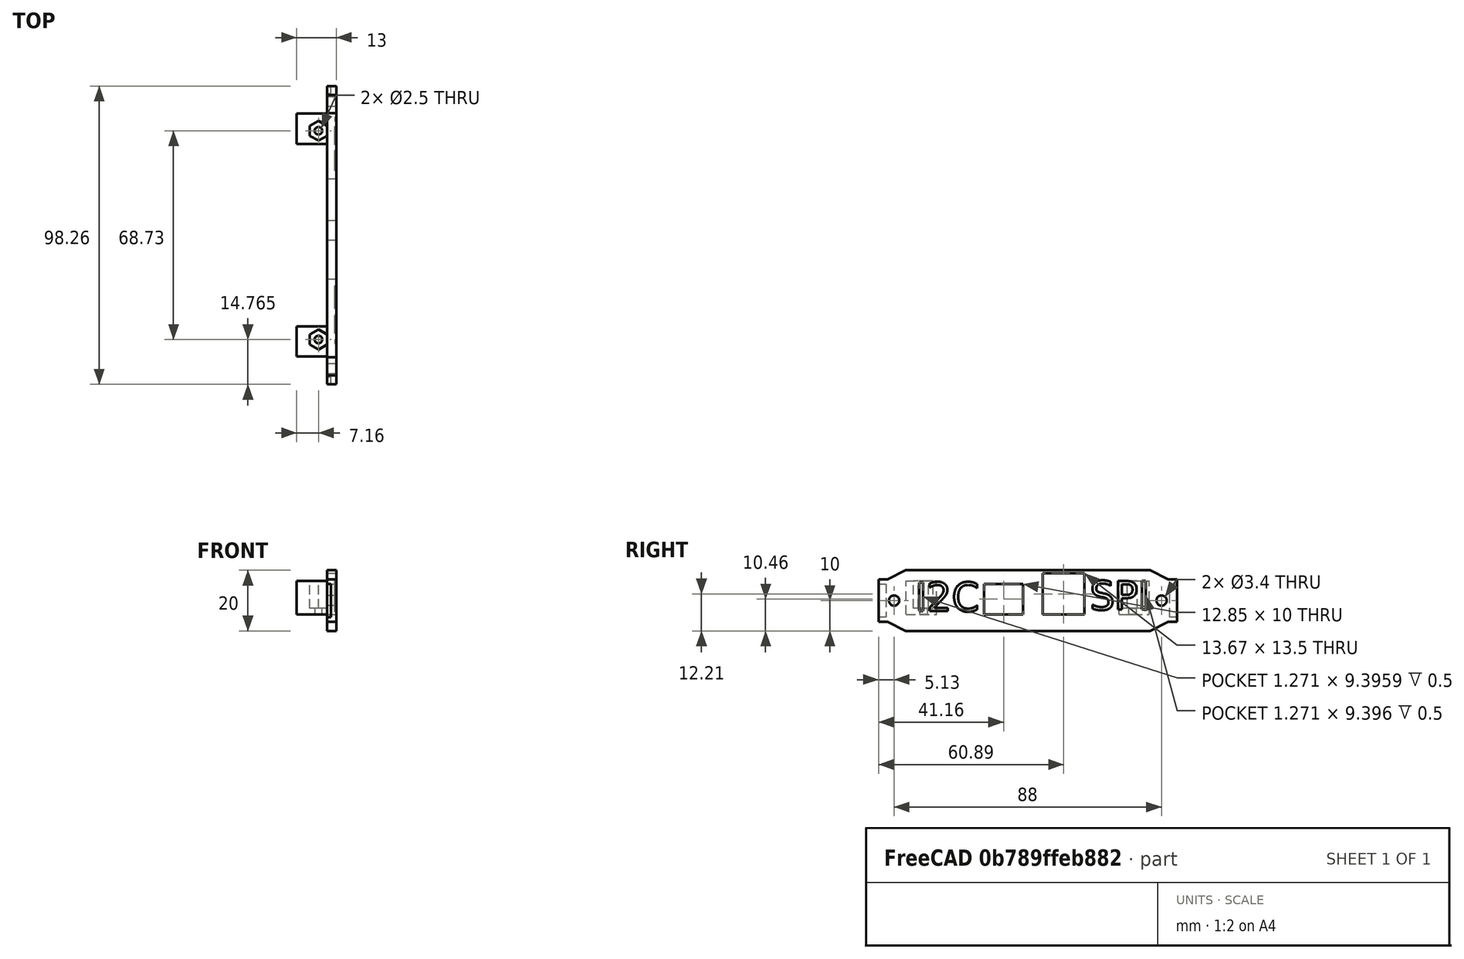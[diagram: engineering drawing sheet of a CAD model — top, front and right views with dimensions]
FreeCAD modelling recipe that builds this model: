
FCSTD DOCUMENT  (FreeCAD 0.19R24291 (Git))
Label: FacePlate_FCNative_v1
License: All rights reserved
LicenseURL: http://en.wikipedia.org/wiki/All_rights_reserved
objects: TechDraw::DrawViewDimension×21, Sketcher::SketchObject×5, PartDesign::Pocket×5, TechDraw::DrawProjGroupItem×4, PartDesign::Pad×2, Part::Part2DObjectPython×2, Mesh::Feature×1, TechDraw::DrawSVGTemplate×1, PartDesign::Body×1, TechDraw::DrawProjGroup×1, TechDraw::DrawPage×1
note: 22 computed .brp shape members not serialized (recipe doc carries the construction recipe); baked Part::Feature solids carry a one-line shape summary decoded from their .brp

FEATURE [Mesh::Feature] PolyVent_SPI_Controller_faceplate_v8  label="PolyVent_SPI_Controller-faceplate v8"
  Placement = pos=(-198.5,104.98,-6.2) rot=(0,0,1;0rad)
FEATURE [Sketcher::SketchObject] Sketch  label="SketchFacePlateBlank"
  FullyConstrained = false
  MapMode = 5
  Placement = pos=(0,0,0) rot=(0.57735,0.57735,0.57735;2.0944rad)
  Support = -> [YZ_Plane]
  sketch-geometry (43):
    g0: Circle CenterX=-44 CenterY=0 CenterZ=0 NormalX=0 NormalY=0 NormalZ=1 AngleXU=0 Radius=1.7
    g1: Circle CenterX=44 CenterY=0 CenterZ=0 NormalX=0 NormalY=0 NormalZ=1 AngleXU=0 Radius=1.7
    g2: LineSegment StartX=-49.13 StartY=6.957 StartZ=0 EndX=-49.13 EndY=-6.957 EndZ=0
    g3: LineSegment StartX=-49.13 StartY=6.957 StartZ=0 EndX=-46.13 EndY=6.957 EndZ=0
    g4: LineSegment StartX=-46.13 StartY=6.957 StartZ=0 EndX=-40.2064 EndY=10 EndZ=0
    g5: LineSegment StartX=-49.13 StartY=-6.957 StartZ=0 EndX=-46.13 EndY=-6.957 EndZ=0
    g6: LineSegment StartX=-46.13 StartY=-6.957 StartZ=0 EndX=-40.2064 EndY=-10 EndZ=0
    g7: LineSegment StartX=-40.2064 StartY=10 StartZ=0 EndX=40.2064 EndY=10 EndZ=0
    g8: LineSegment StartX=40.2064 StartY=10 StartZ=0 EndX=46.13 EndY=6.957 EndZ=0
    g9: LineSegment StartX=46.13 StartY=6.957 StartZ=0 EndX=49.13 EndY=6.957 EndZ=0
    g10: LineSegment StartX=49.13 StartY=6.957 StartZ=0 EndX=49.13 EndY=-6.957 EndZ=0
    g11: LineSegment StartX=49.13 StartY=-6.957 StartZ=0 EndX=46.13 EndY=-6.957 EndZ=0
    g12: LineSegment StartX=46.13 StartY=-6.957 StartZ=0 EndX=40.2064 EndY=-10 EndZ=0
    g13: LineSegment StartX=40.2064 StartY=-10 StartZ=0 EndX=-40.2064 EndY=-10 EndZ=0
    g14: ArcOfCircle CenterX=-46.13 CenterY=-6.957 CenterZ=0 NormalX=0 NormalY=0 NormalZ=1 AngleXU=0 Radius=3 StartAngle=3.14159 EndAngle=5.80863
    g15: LineSegment StartX=-40 StartY=-4.54 StartZ=0 EndX=40 EndY=-4.54 EndZ=0
    g16: LineSegment StartX=40 StartY=-4.54 StartZ=0 EndX=40 EndY=-6.14 EndZ=0
    g17: LineSegment StartX=40 StartY=-6.14 StartZ=0 EndX=-40 EndY=-6.14 EndZ=0
    g18: LineSegment StartX=-40 StartY=-6.14 StartZ=0 EndX=-40 EndY=-4.54 EndZ=0
    g19: LineSegment StartX=-40 StartY=-4.54 StartZ=0 EndX=-30 EndY=-4.54 EndZ=0
    g20: LineSegment StartX=-30 StartY=-4.54 StartZ=0 EndX=-30 EndY=6.46 EndZ=0
    g21: LineSegment StartX=-30 StartY=6.46 StartZ=0 EndX=-40 EndY=6.46 EndZ=0
    g22: LineSegment StartX=-40 StartY=6.46 StartZ=0 EndX=-40 EndY=-4.54 EndZ=0
    g23: LineSegment StartX=40 StartY=-4.54 StartZ=0 EndX=30 EndY=-4.54 EndZ=0
    g24: LineSegment StartX=30 StartY=-4.54 StartZ=0 EndX=30 EndY=6.46 EndZ=0
    g25: LineSegment StartX=30 StartY=6.46 StartZ=0 EndX=40 EndY=6.46 EndZ=0
    g26: LineSegment StartX=40 StartY=6.46 StartZ=0 EndX=40 EndY=-4.54 EndZ=0
    g27: LineSegment StartX=31.113 StartY=6.46 StartZ=0 EndX=37.637 EndY=6.46 EndZ=0
    g28: LineSegment StartX=37.637 StartY=6.46 StartZ=0 EndX=37.637 EndY=-2.54 EndZ=0
    g29: LineSegment StartX=37.637 StartY=-2.54 StartZ=0 EndX=31.113 EndY=-2.54 EndZ=0
    g30: LineSegment StartX=31.113 StartY=-2.54 StartZ=0 EndX=31.113 EndY=6.46 EndZ=0
    g31: LineSegment StartX=34.375 StartY=6.46 StartZ=0 EndX=34.375 EndY=-4.54 EndZ=0
    g32: LineSegment StartX=-34.375 StartY=6.46 StartZ=0 EndX=-34.375 EndY=-4.54 EndZ=0
    g33: LineSegment StartX=37.637 StartY=18.8909 StartZ=0 EndX=36.006 EndY=21.7159 EndZ=0
    g34: LineSegment StartX=36.006 StartY=21.7159 StartZ=0 EndX=32.744 EndY=21.7159 EndZ=0
    g35: LineSegment StartX=32.744 StartY=21.7159 StartZ=0 EndX=31.113 EndY=18.8909 EndZ=0
    g36: LineSegment StartX=31.113 StartY=18.8909 StartZ=0 EndX=32.744 EndY=16.0659 EndZ=0
    g37: LineSegment StartX=32.744 StartY=16.0659 StartZ=0 EndX=36.006 EndY=16.0659 EndZ=0
    g38: LineSegment StartX=36.006 StartY=16.0659 StartZ=0 EndX=37.637 EndY=18.8909 EndZ=0
    g39: Circle CenterX=34.375 CenterY=18.8909 CenterZ=0 NormalX=0 NormalY=0 NormalZ=1 AngleXU=0 Radius=3.26203
    g40: LineSegment StartX=-49.13 StartY=5.46 StartZ=0 EndX=-46.63 EndY=5.46 EndZ=0
    g41: LineSegment StartX=-46.63 StartY=5.46 StartZ=0 EndX=-46.63 EndY=-5.46 EndZ=0
    g42: LineSegment StartX=-46.63 StartY=-5.46 StartZ=0 EndX=-49.13 EndY=-5.46 EndZ=0
  constraints (119):
    c: Vertical(g2)
    c: Coincident(g3,g2)
    c: Horizontal(g3)
    c: Coincident(g4,g3)
    c: Coincident(g5,g2)
    c: Horizontal(g5)
    c: Coincident(g6,g5)
    c: Vertical(g4,g6)
    c: Vertical(g5,g3)
    c: Coincident(g7,g4)
    c: Horizontal(g7)
    c: Coincident(g8,g7)
    c: Coincident(g9,g8)
    c: Horizontal(g9)
    c: Coincident(g10,g9)
    c: Vertical(g10)
    c: Coincident(g11,g10)
    c: Horizontal(g11)
    c: Coincident(g12,g11)
    c: Coincident(g13,g12)
    c: Coincident(g13,g6)
    c: Horizontal(g13)
    c: Equal(g6,g4)
    c: Equal(g4,g8)
    c: Equal(g8,g12)
    c: Equal(g5,g11)
    c: Vertical(g11,g8)
    c: Horizontal(g0,g1)
    c: Horizontal(g5,g11)
    c: Horizontal(g3,g8)
    c: DistanceY(g5) = -6.957
    c: DistanceX(g5,g5) = 3
    c: DistanceY(g2,g2) = 13.914
    c: DistanceX(g5,g6) = 5.92358
    c: DistanceY(g6,g4) = 20
    c: Coincident(g14,g5)
    c: PointOnObject(g14,g6)
    c: Angle(g14) = 2.66704
    c: Diameter(g0) = 3.4
    c: Equal(g1,g0)
    c: DistanceX(g2,g10) = 98.26  'L1'
    c: PointOnObject(g1,g-1)
    c: Coincident(g15,g16)
    c: Coincident(g16,g17)
    c: Coincident(g17,g18)
    c: Coincident(g18,g15)
    c: Horizontal(g15)
    c: Vertical(g16)
    c: Vertical(g18)
    c: DistanceY(g15) = -4.54  'PCB_top_center_offset'
    c: DistanceY(g16,g16) = 1.6  'PCB_tickness'
    c: DistanceX(g17,g17) = 80  'PCB_width'
    c: Symmetric(g16,g17,g-2)
    c: Coincident(g14,g2)
    c: Coincident(g19,g20)
    c: Coincident(g20,g21)
    c: Coincident(g21,g22)
    c: Coincident(g22,g19)
    c: Horizontal(g19)
    c: Horizontal(g21)
    c: Vertical(g20)
    c: Vertical(g22)
    c: Coincident(g19,g15)
    c: Coincident(g23,g24)
    c: Coincident(g24,g25)
    c: Coincident(g25,g26)
    c: Coincident(g26,g23)
    c: Horizontal(g23)
    c: Horizontal(g25)
    c: Vertical(g24)
    c: Vertical(g26)
    c: Coincident(g23,g15)
    c: Horizontal(g20,g24)
    c: Equal(g21,g25)
    c: DistanceY(g26,g26) = 11  'PCB_mounting_tab_height'
    c: DistanceX(g25,g25) = 10  'PCB_mount_tab_width'
    c: Coincident(g27,g28)
    c: Coincident(g28,g29)
    c: Coincident(g29,g30)
    c: Coincident(g30,g27)
    c: Horizontal(g27)
    c: Vertical(g28)
    c: Vertical(g30)
    c: PointOnObject(g27,g25)
    c: DistanceY(g23,g29) = 2  'bore_length'
    c: PointOnObject(g31,g25)
    c: PointOnObject(g31,g15)
    c: Vertical(g31)
    c: Symmetric(g29,g28,g31)
    c: PointOnObject(g32,g21)
    c: Vertical(g32)
    c: Symmetric(g32,g31,g-2)
    c: DistanceX(g32,g31) = 68.75  'PCB_hole_distance_width'
    c: Coincident(g33,g34)
    c: Coincident(g34,g35)
    c: Coincident(g35,g36)
    c: Coincident(g36,g37)
    c: Coincident(g37,g38)
    c: Coincident(g38,g33)
    c: Equal(g33, g34-g38) x5
    c: PointOnObject(g33,g39)
    c: PointOnObject(g34,g39)
    c: PointOnObject(g35,g39)
    c: PointOnObject(g36,g39)
    c: PointOnObject(g37,g39)
    c: PointOnObject(g38,g39)
    c: Vertical(g27,g35)
    c: Horizontal(g35,g33)
    c: Vertical(g33,g27)
    c: DistanceY(g37,g33) = 5.65  'nut_spanner_dim'
    c: PointOnObject(g40,g2)
    c: Horizontal(g40)
    c: Coincident(g41,g40)
    c: Coincident(g42,g41)
    c: PointOnObject(g42,g2)
    c: Horizontal(g42)
    c: DistanceX(g42,g42) = 2.5  'L3'
    c: Symmetric(g41,g40,g-1)
    c: DistanceY(g41,g41) = 10.92  'L2'
FEATURE [PartDesign::Pad] Pad  label="PadFacePlateBlank"
  Direction = (1,-2e-16,3e-16)
  Length = 3
  Length2 = 10
  Placement = pos=(0,0,0) rot=(0.57735,0.57735,0.57735;2.0944rad)
  Profile = -> Sketch
  Type = 0
FEATURE [Sketcher::SketchObject] Sketch001  label="SketchPCBMount"
  AttachmentOffset = pos=(0,0,-4.54) rot=(0,0,1;0rad)
  FullyConstrained = false
  MapMode = 5
  Placement = pos=(0,0,-4.54) rot=(0,0,1;0rad)
  Support = -> [XY_Plane]
  expr: .AttachmentOffset.Base.z = Sketch.Constraints.PCB_top_center_offset
  expr: Constraints[20] = Sketch.Constraints.PCB_mount_tab_width
  expr: Constraints[39] = Sketch.Constraints.PCB_width
  sketch-geometry (15):
    g0: LineSegment StartX=0 StartY=40 StartZ=0 EndX=-10 EndY=40 EndZ=0
    g1: LineSegment StartX=-10 StartY=40 StartZ=0 EndX=-10 EndY=30 EndZ=0
    g2: LineSegment StartX=-10 StartY=30 StartZ=0 EndX=0 EndY=30 EndZ=0
    g3: LineSegment StartX=0 StartY=30 StartZ=0 EndX=0 EndY=40 EndZ=0
    g4: LineSegment StartX=0 StartY=-30 StartZ=0 EndX=-10 EndY=-30 EndZ=0
    g5: LineSegment StartX=-10 StartY=-30 StartZ=0 EndX=-10 EndY=-40 EndZ=0
    g6: LineSegment StartX=-10 StartY=-40 StartZ=0 EndX=0 EndY=-40 EndZ=0
    g7: LineSegment StartX=0 StartY=-40 StartZ=0 EndX=0 EndY=-30 EndZ=0
    g8: Circle CenterX=-2.84 CenterY=-34.365 CenterZ=0 NormalX=0 NormalY=0 NormalZ=1 AngleXU=0 Radius=1.25
    g9: Circle CenterX=-2.84 CenterY=34.365 CenterZ=0 NormalX=0 NormalY=0 NormalZ=1 AngleXU=0 Radius=1.25
    g10: LineSegment StartX=0 StartY=0 StartZ=0 EndX=-11.2307 EndY=0 EndZ=0
    g11: LineSegment StartX=-136.907 StartY=40 StartZ=0 EndX=-12.6927 EndY=40 EndZ=0
    g12: LineSegment StartX=-12.6927 StartY=40 StartZ=0 EndX=-12.6927 EndY=-40 EndZ=0
    g13: LineSegment StartX=-12.6927 StartY=-40 StartZ=0 EndX=-136.907 EndY=-40 EndZ=0
    g14: LineSegment StartX=-136.907 StartY=-40 StartZ=0 EndX=-136.907 EndY=40 EndZ=0
  constraints (40):
    c: Coincident(g0,g1)
    c: Coincident(g1,g2)
    c: Coincident(g2,g3)
    c: Coincident(g3,g0)
    c: Horizontal(g0)
    c: Horizontal(g2)
    c: Vertical(g1)
    c: Vertical(g3)
    c: PointOnObject(g0,g-2)
    c: Coincident(g4,g5)
    c: Coincident(g5,g6)
    c: Coincident(g6,g7)
    c: Coincident(g7,g4)
    c: Horizontal(g4)
    c: Horizontal(g6)
    c: Vertical(g5)
    c: Vertical(g7)
    c: PointOnObject(g4,g-2)
    c: Equal(g8,g9)
    c: DistanceX(g2,g2) = 10
    c: DistanceY(g1,g1) = 10
    c: Diameter(g9) = 2.5
    c: PointOnObject(g10,g-2)
    c: Symmetric(g8,g9,g10)
    c: Horizontal(g10)
    c: DistanceX(g8,g10) = 2.84
    c: DistanceY(g8,g9) = 68.73
    c: DistanceY(g4,g1) = 60
    c: Symmetric(g4,g1,g10)
    c: Equal(g1,g5)
    c: PointOnObject(g10,g-1)
    c: Coincident(g11,g12)
    c: Coincident(g12,g13)
    c: Coincident(g13,g14)
    c: Coincident(g14,g11)
    c: Horizontal(g11)
    c: Horizontal(g13)
    c: Vertical(g12)
    c: Symmetric(g13,g11,g-1)
    c: DistanceY(g14,g14) = 80
FEATURE [PartDesign::Pad] Pad001  label="PadPCBMount"
  BaseFeature = -> Pad
  Direction = (0,0,1)
  Length = 11
  Length2 = 10
  Placement = pos=(0,0,0) rot=(0.57735,0.57735,0.57735;2.0944rad)
  Profile = -> Sketch001
  Type = 0
  expr: Length = Sketch.Constraints.PCB_mounting_tab_height
FEATURE [Sketcher::SketchObject] Sketch002  label="SketchNuts"
  AttachmentOffset = pos=(0,0,-2.54) rot=(0,0,1;0rad)
  FullyConstrained = false
  MapMode = 5
  Placement = pos=(0,0,-2.54) rot=(0,0,1;0rad)
  Support = -> [XY_Plane]
  expr: .AttachmentOffset.Base.z = Sketch.Constraints.PCB_top_center_offset + Sketch.Constraints.bore_length
  expr: Constraints[18] = Sketch.Constraints.nut_spanner_dim
  expr: Constraints[50] = Sketch.Constraints.PCB_hole_distance_width
  expr: Constraints[51] = Sketch.Constraints.PCB_width
  sketch-geometry (18):
    g0: LineSegment StartX=-0.015 StartY=36.006 StartZ=0 EndX=-2.84 EndY=37.637 EndZ=0
    g1: LineSegment StartX=-2.84 StartY=37.637 StartZ=0 EndX=-5.665 EndY=36.006 EndZ=0
    g2: LineSegment StartX=-5.665 StartY=36.006 StartZ=0 EndX=-5.665 EndY=32.744 EndZ=0
    g3: LineSegment StartX=-5.665 StartY=32.744 StartZ=0 EndX=-2.84 EndY=31.113 EndZ=0
    g4: LineSegment StartX=-2.84 StartY=31.113 StartZ=0 EndX=-0.015 EndY=32.744 EndZ=0
    g5: LineSegment StartX=-0.015 StartY=32.744 StartZ=0 EndX=-0.015 EndY=36.006 EndZ=0
    g6: Circle CenterX=-2.84 CenterY=34.375 CenterZ=0 NormalX=0 NormalY=0 NormalZ=1 AngleXU=0 Radius=3.26203
    g7: LineSegment StartX=-73.2053 StartY=40 StartZ=0 EndX=0 EndY=40 EndZ=0
    g8: LineSegment StartX=0 StartY=40 StartZ=0 EndX=0 EndY=-40 EndZ=0
    g9: LineSegment StartX=0 StartY=-40 StartZ=0 EndX=-73.2053 EndY=-40 EndZ=0
    g10: LineSegment StartX=-73.2053 StartY=-40 StartZ=0 EndX=-73.2053 EndY=40 EndZ=0
    g11: LineSegment StartX=-0.015 StartY=-36.006 StartZ=0 EndX=-0.015 EndY=-32.744 EndZ=0
    g12: LineSegment StartX=-0.015 StartY=-32.744 StartZ=0 EndX=-2.84 EndY=-31.113 EndZ=0
    g13: LineSegment StartX=-2.84 StartY=-31.113 StartZ=0 EndX=-5.665 EndY=-32.744 EndZ=0
    g14: LineSegment StartX=-5.665 StartY=-32.744 StartZ=0 EndX=-5.665 EndY=-36.006 EndZ=0
    g15: LineSegment StartX=-5.665 StartY=-36.006 StartZ=0 EndX=-2.84 EndY=-37.637 EndZ=0
    g16: LineSegment StartX=-2.84 StartY=-37.637 StartZ=0 EndX=-0.015 EndY=-36.006 EndZ=0
    g17: Circle CenterX=-2.84 CenterY=-34.375 CenterZ=0 NormalX=0 NormalY=0 NormalZ=1 AngleXU=0 Radius=3.26203
  constraints (45):
    c: Coincident(g0,g1)
    c: Coincident(g1,g2)
    c: Coincident(g2,g3)
    c: Coincident(g3,g4)
    c: Coincident(g4,g5)
    c: Coincident(g5,g0)
    c: Equal(g0, g1-g5) x5
    c: PointOnObject(g0,g6)
    c: PointOnObject(g1,g6)
    c: PointOnObject(g2,g6)
    c: PointOnObject(g3,g6)
    c: PointOnObject(g4,g6)
    c: PointOnObject(g5,g6)
    c: Vertical(g5)
    c: DistanceX(g2,g4) = 5.65
    c: DistanceY(g-1,g6) = 34.375
    c: DistanceX(g6,g-1) = 2.84
    c: Coincident(g7,g8)
    c: Coincident(g8,g9)
    c: Coincident(g9,g10)
    c: Coincident(g10,g7)
    c: Horizontal(g7)
    c: Horizontal(g9)
    c: Vertical(g8)
    c: PointOnObject(g8,g-2)
    c: Symmetric(g9,g7,g-1)
    c: Coincident(g11,g12)
    c: Coincident(g12,g13)
    c: Coincident(g13,g14)
    c: Coincident(g14,g15)
    c: Coincident(g15,g16)
    c: Coincident(g16,g11)
    c: Equal(g11, g12-g16) x5
    c: PointOnObject(g11,g17)
    c: PointOnObject(g12,g17)
    c: PointOnObject(g13,g17)
    c: PointOnObject(g14,g17)
    c: PointOnObject(g15,g17)
    c: PointOnObject(g16,g17)
    c: Vertical(g11)
    c: Equal(g17,g6)
    c: Symmetric(g17,g6,g-1)
    c: DistanceY(g17,g6) = 68.75
    c: DistanceY(g10,g10) = 80
    c: DistanceY(g6,g7) = 5.625
FEATURE [PartDesign::Pocket] Pocket  label="Pocket_nut"
  BaseFeature = -> Pad001
  Length = 5
  Length2 = 5
  Placement = pos=(0,0,0) rot=(0.57735,0.57735,0.57735;2.0944rad)
  Profile = -> Sketch002
  Reversed = true
  Type = 1
FEATURE [Sketcher::SketchObject] Sketch003  label="SketchExtraction"
  FullyConstrained = true
  MapMode = 5
  Placement = pos=(0,0,0) rot=(0.57735,0.57735,0.57735;2.0944rad)
  Support = -> [YZ_Plane]
  expr: Constraints[19] = Sketch.Constraints.L1
  expr: Constraints[20] = Sketch.Constraints.L2
  expr: Constraints[21] = Sketch.Constraints.L3
  sketch-geometry (8):
    g0: LineSegment StartX=-49.13 StartY=5.46 StartZ=0 EndX=-46.63 EndY=5.46 EndZ=0
    g1: LineSegment StartX=-46.63 StartY=5.46 StartZ=0 EndX=-46.63 EndY=-5.46 EndZ=0
    g2: LineSegment StartX=-46.63 StartY=-5.46 StartZ=0 EndX=-49.13 EndY=-5.46 EndZ=0
    g3: LineSegment StartX=-49.13 StartY=-5.46 StartZ=0 EndX=-49.13 EndY=5.46 EndZ=0
    g4: LineSegment StartX=46.63 StartY=5.46 StartZ=0 EndX=49.13 EndY=5.46 EndZ=0
    g5: LineSegment StartX=49.13 StartY=5.46 StartZ=0 EndX=49.13 EndY=-5.46 EndZ=0
    g6: LineSegment StartX=49.13 StartY=-5.46 StartZ=0 EndX=46.63 EndY=-5.46 EndZ=0
    g7: LineSegment StartX=46.63 StartY=-5.46 StartZ=0 EndX=46.63 EndY=5.46 EndZ=0
  constraints (22):
    c: Coincident(g0,g1)
    c: Coincident(g1,g2)
    c: Coincident(g2,g3)
    c: Coincident(g3,g0)
    c: Horizontal(g0)
    c: Horizontal(g2)
    c: Vertical(g1)
    c: Coincident(g4,g5)
    c: Coincident(g5,g6)
    c: Coincident(g6,g7)
    c: Coincident(g7,g4)
    c: Horizontal(g4)
    c: Horizontal(g6)
    c: Vertical(g5)
    c: Vertical(g7)
    c: Horizontal(g0,g4)
    c: Symmetric(g0,g5,g-1)
    c: Symmetric(g2,g0,g-1)
    c: Equal(g0,g4)
    c: DistanceX(g2,g5) = 98.26
    c: DistanceY(g1,g1) = 10.92
    c: DistanceX(g2,g2) = 2.5
FEATURE [PartDesign::Pocket] Pocket001  label="PocketExtraction"
  BaseFeature = -> Pocket
  Length = 1.25
  Length2 = 5
  Placement = pos=(0,0,0) rot=(0.57735,0.57735,0.57735;2.0944rad)
  Profile = -> Sketch003
  Reversed = true
  Type = 0
FEATURE [TechDraw::DrawSVGTemplate] Template
  EditableTexts = Approved1=20230622 1317; Approved2=Approved 2; CheckedBy=Checked By; Code=Code; CompanyAddress=Publnv.org; CompanyName=PUblicInvention; DrawingNumber=Drawing Number; DrawingTitle1=PolyVentFacePlate; DrawingTitle2=FacePlate_FCNative_v1_SPI_Controller.p[df; DrawingTitle3=Drawing Title 3; DrawnBy=(Forrest) Lee Erickson; Revision=Rev; Scale=Scale 1:1; Sheet=Sheet 1 of 1
  Height = 215.9
  Orientation = 1
  Width = 279.4
FEATURE [Sketcher::SketchObject] Sketch004  label="SketchFacePlateHoles"
  FullyConstrained = false
  MapMode = 5
  Placement = pos=(0,0,0) rot=(0.57735,0.57735,0.57735;2.0944rad)
  Support = -> [YZ_Plane]
  sketch-geometry (11):
    g0: GeomPoint X=0 Y=0 Z=0
    g1: LineSegment StartX=4.925 StartY=8.96 StartZ=0 EndX=18.595 EndY=8.96 EndZ=0
    g2: LineSegment StartX=18.595 StartY=8.96 StartZ=0 EndX=18.595 EndY=-4.54 EndZ=0
    g3: LineSegment StartX=18.595 StartY=-4.54 StartZ=0 EndX=4.925 EndY=-4.54 EndZ=0
    g4: LineSegment StartX=4.925 StartY=-4.54 StartZ=0 EndX=4.925 EndY=8.96 EndZ=0
    g5: LineSegment StartX=-14.395 StartY=5.46 StartZ=0 EndX=-1.545 EndY=5.46 EndZ=0
    g6: LineSegment StartX=-1.545 StartY=5.46 StartZ=0 EndX=-1.545 EndY=-4.54 EndZ=0
    g7: LineSegment StartX=-1.545 StartY=-4.54 StartZ=0 EndX=-14.395 EndY=-4.54 EndZ=0
    g8: LineSegment StartX=-14.395 StartY=-4.54 StartZ=0 EndX=-14.395 EndY=5.46 EndZ=0
    g9: GeomPoint X=-7.97 Y=0.46 Z=0
    g10: GeomPoint X=11.76 Y=2.21 Z=0
  constraints (27):
    c: Coincident(g1,g2)
    c: Coincident(g2,g3)
    c: Coincident(g3,g4)
    c: Coincident(g4,g1)
    c: Horizontal(g1)
    c: Horizontal(g3)
    c: Vertical(g2)
    c: Vertical(g4)
    c: Coincident(g5,g6)
    c: Coincident(g6,g7)
    c: Coincident(g7,g8)
    c: Coincident(g8,g5)
    c: Horizontal(g5)
    c: Horizontal(g7)
    c: Vertical(g6)
    c: Vertical(g8)
    c: PointOnObject(g0,g-2)
    c: Symmetric(g7,g5,g9)
    c: Symmetric(g3,g1,g10)
    c: Horizontal(g6,g3)
    c: DistanceX(g5,g5) = 12.85
    c: DistanceY(g8,g8) = 10
    c: DistanceX(g1,g1) = 13.67
    c: DistanceY(g2,g2) = 13.5
    c: DistanceX(g9,g0) = 7.97
    c: DistanceX(g0,g10) = 11.76
    c: DistanceY(g6,g-1) = 4.54
FEATURE [PartDesign::Pocket] Pocket002  label="PocketFacePlateHoles"
  BaseFeature = -> Pocket001
  Length = 5
  Length2 = 100
  Placement = pos=(0,0,0) rot=(0.57735,0.57735,0.57735;2.0944rad)
  Profile = -> Sketch004
  Reversed = true
  Type = 1
FEATURE [Part::Part2DObjectPython] ShapeString  label="ShapeStringSPI"  # Draft 2D object (typed FeaturePython)
  FontFile = <path>
  Placement = pos=(3,20.3978,-2.95812) rot=(0.57735,0.57735,0.57735;2.0944rad)
  Size = 10
  String = SPI
  Tracking = 0
FEATURE [PartDesign::Pocket] Pocket003  label="PocketSPI"
  BaseFeature = -> Pocket002
  Length = 0.5
  Length2 = 100
  Placement = pos=(0,0,0) rot=(0.57735,0.57735,0.57735;2.0944rad)
  Profile = -> ShapeString
  Type = 0
FEATURE [Part::Part2DObjectPython] ShapeString001  label="ShapeStringI2C"  # Draft 2D object (typed FeaturePython)
  FontFile = <path>
  Placement = pos=(3,-37.0721,-3.45493) rot=(0.57735,0.57735,0.57735;2.0944rad)
  Size = 10
  String = I2C
  Tracking = 0
FEATURE [PartDesign::Pocket] Pocket004  label="PocketI2C"
  BaseFeature = -> Pocket003
  Length = 0.5
  Length2 = 100
  Placement = pos=(0,0,0) rot=(0.57735,0.57735,0.57735;2.0944rad)
  Profile = -> ShapeString001
  Type = 0
FEATURE [PartDesign::Body] Body
  Group = -> [Sketch,Pad,Sketch001,Pad001,Sketch002,Pocket,Sketch003,Pocket001,Sketch004,Pocket002,ShapeString,Pocket003,ShapeString001,Pocket004]
  Origin = -> Origin
  Tip = -> Pocket004
FEATURE [TechDraw::DrawProjGroupItem] ProjItem  label="Front"
  CoarseView = false
  Direction = (1,0,0)
  Focus = 100
  HardHidden = false
  IsoCount = 0
  IsoHidden = false
  IsoVisible = false
  LockPosition = true
  Perspective = false
  Rotation = 0
  RotationVector = (0,1,0)
  ScaleType = 2
  SeamHidden = false
  SeamVisible = true
  SmoothHidden = false
  SmoothVisible = true
  Source = -> [Body]
  Type = 0
  X = 0
  XDirection = (0,1,0)
  Y = 0
FEATURE [TechDraw::DrawProjGroupItem] ProjItem001  label="FrontTopRight"
  CoarseView = false
  Direction = (0.57735,0.57735,0.57735)
  Focus = 100
  HardHidden = false
  IsoCount = 0
  IsoHidden = false
  IsoVisible = false
  LockPosition = true
  Perspective = false
  Rotation = 0
  RotationVector = (1,0,0)
  ScaleType = 2
  SeamHidden = false
  SeamVisible = true
  SmoothHidden = false
  SmoothVisible = true
  Source = -> [Body]
  Type = 7
  X = 115.005
  XDirection = (-0.707107,0.707107,0)
  Y = 72.8098
FEATURE [TechDraw::DrawProjGroupItem] ProjItem002  label="Top"
  CoarseView = false
  Direction = (0,0,1)
  Focus = 100
  HardHidden = false
  IsoCount = 0
  IsoHidden = false
  IsoVisible = false
  LockPosition = true
  Perspective = false
  Rotation = 0
  RotationVector = (1,0,0)
  ScaleType = 2
  SeamHidden = false
  SeamVisible = true
  SmoothHidden = false
  SmoothVisible = true
  Source = -> [Body]
  Type = 4
  X = 0
  XDirection = (0,1,0)
  Y = 69.929
FEATURE [TechDraw::DrawProjGroupItem] ProjItem003  label="Right"
  CoarseView = false
  Direction = (1e-16,1,0)
  Focus = 100
  HardHidden = false
  IsoCount = 0
  IsoHidden = false
  IsoVisible = false
  LockPosition = true
  Perspective = false
  Rotation = 0
  RotationVector = (1,0,0)
  ScaleType = 2
  SeamHidden = false
  SeamVisible = true
  SmoothHidden = false
  SmoothVisible = true
  Source = -> [Body]
  Type = 2
  X = 103.269
  XDirection = (-1,1e-16,0)
  Y = 0
FEATURE [TechDraw::DrawProjGroup] ProjGroup
  Anchor = -> ProjItem
  AutoDistribute = false
  LockPosition = true
  ProjectionType = 0
  Rotation = 0
  ScaleType = 2
  Source = -> [Body]
  Views = -> [ProjItem,ProjItem001,ProjItem002,ProjItem003]
  X = 92.2805
  Y = 95.7586
  spacingX = 15
  spacingY = 15
FEATURE [TechDraw::DrawViewDimension] Dimension
  Arbitrary = false
  ArbitraryTolerances = false
  EqualTolerance = true
  FormatSpec = %.3f
  FormatSpecOverTolerance = %+.3f
  FormatSpecUnderTolerance = %+.3f
  Inverted = false
  LockPosition = false
  MeasureType = 1
  OverTolerance = 0
  References2D = -> [ProjItem]
  Rotation = 0
  ScaleType = 2
  TheoreticalExact = false
  Type = 1
  UnderTolerance = 0
  X = 0.841435
  Y = -24.3466
FEATURE [TechDraw::DrawViewDimension] Dimension003
  Arbitrary = false
  ArbitraryTolerances = false
  EqualTolerance = true
  FormatSpec = %.3f
  FormatSpecOverTolerance = %+.3f
  FormatSpecUnderTolerance = %+.3f
  Inverted = false
  LockPosition = false
  MeasureType = 1
  OverTolerance = 0
  References2D = -> [ProjItem]
  Rotation = 0
  ScaleType = 2
  TheoreticalExact = false
  Type = 2
  UnderTolerance = 0
  X = 62.439
  Y = 8.59694
FEATURE [TechDraw::DrawViewDimension] Dimension004
  Arbitrary = false
  ArbitraryTolerances = false
  EqualTolerance = true
  FormatSpec = %.3f
  FormatSpecOverTolerance = %+.3f
  FormatSpecUnderTolerance = %+.3f
  Inverted = false
  LockPosition = false
  MeasureType = 1
  OverTolerance = 0
  References2D = -> [ProjItem002]
  Rotation = 0
  ScaleType = 2
  TheoreticalExact = false
  Type = 2
  UnderTolerance = 0
  X = -61.2663
  Y = -3.72413
FEATURE [TechDraw::DrawViewDimension] Dimension005
  Arbitrary = false
  ArbitraryTolerances = false
  EqualTolerance = true
  FormatSpec = %.3f
  FormatSpecOverTolerance = %+.3f
  FormatSpecUnderTolerance = %+.3f
  Inverted = false
  LockPosition = false
  MeasureType = 1
  OverTolerance = 0
  References2D = -> [ProjItem002]
  Rotation = 0
  ScaleType = 2
  TheoreticalExact = false
  Type = 1
  UnderTolerance = 0
  X = -2.34704
  Y = 15.7693
FEATURE [TechDraw::DrawViewDimension] Dimension006
  Arbitrary = false
  ArbitraryTolerances = false
  EqualTolerance = true
  FormatSpec = %.3f
  FormatSpecOverTolerance = %+.3f
  FormatSpecUnderTolerance = %+.3f
  Inverted = false
  LockPosition = false
  MeasureType = 1
  OverTolerance = 0
  References2D = -> [ProjItem002]
  Rotation = 0
  ScaleType = 2
  TheoreticalExact = false
  Type = 1
  UnderTolerance = 0
  X = -0.57033
  Y = 29.9708
FEATURE [TechDraw::DrawViewDimension] Dimension007
  Arbitrary = false
  ArbitraryTolerances = false
  EqualTolerance = true
  FormatSpec = %.3f
  FormatSpecOverTolerance = %+.3f
  FormatSpecUnderTolerance = %+.3f
  Inverted = false
  LockPosition = false
  MeasureType = 1
  OverTolerance = 0
  References2D = -> [ProjItem002]
  Rotation = 0
  ScaleType = 2
  TheoreticalExact = false
  Type = 1
  UnderTolerance = 0
  X = 13.5967
  Y = 22.9686
FEATURE [TechDraw::DrawViewDimension] Dimension008
  Arbitrary = false
  ArbitraryTolerances = false
  EqualTolerance = true
  FormatSpec = %.3f
  FormatSpecOverTolerance = %+.3f
  FormatSpecUnderTolerance = %+.3f
  Inverted = false
  LockPosition = false
  MeasureType = 1
  OverTolerance = 0
  References2D = -> [ProjItem002]
  Rotation = 0
  ScaleType = 2
  TheoreticalExact = false
  Type = 2
  UnderTolerance = 0
  X = 49.4735
  Y = 16.3503
FEATURE [TechDraw::DrawViewDimension] Dimension009
  Arbitrary = false
  ArbitraryTolerances = false
  EqualTolerance = true
  FormatSpec = ⌀%.3f
  FormatSpecOverTolerance = %+.3f
  FormatSpecUnderTolerance = %+.3f
  Inverted = false
  LockPosition = false
  MeasureType = 1
  OverTolerance = 0
  References2D = -> [ProjItem002]
  Rotation = 0
  ScaleType = 2
  TheoreticalExact = false
  Type = 5
  UnderTolerance = 0
  X = -55.6208
  Y = 21.8383
FEATURE [TechDraw::DrawViewDimension] Dimension010
  Arbitrary = false
  ArbitraryTolerances = false
  EqualTolerance = true
  FormatSpec = %.3f
  FormatSpecOverTolerance = %+.3f
  FormatSpecUnderTolerance = %+.3f
  Inverted = false
  LockPosition = false
  MeasureType = 1
  OverTolerance = 0
  References2D = -> [ProjItem]
  Rotation = 0
  ScaleType = 2
  TheoreticalExact = false
  Type = 1
  UnderTolerance = 0
  X = 7.90009
  Y = 48.7051
FEATURE [TechDraw::DrawViewDimension] Dimension011
  Arbitrary = false
  ArbitraryTolerances = false
  EqualTolerance = true
  FormatSpec = %.3f
  FormatSpecOverTolerance = %+.3f
  FormatSpecUnderTolerance = %+.3f
  Inverted = false
  LockPosition = false
  MeasureType = 1
  OverTolerance = 0
  References2D = -> [ProjItem003]
  Rotation = 0
  ScaleType = 2
  TheoreticalExact = false
  Type = 2
  UnderTolerance = 0
  X = 14.2747
  Y = -11.9666
FEATURE [TechDraw::DrawViewDimension] Dimension017
  Arbitrary = false
  ArbitraryTolerances = false
  EqualTolerance = true
  FormatSpec = %.3f
  FormatSpecOverTolerance = %+.3f
  FormatSpecUnderTolerance = %+.3f
  Inverted = false
  LockPosition = false
  MeasureType = 1
  OverTolerance = 0
  References2D = -> [ProjItem003]
  Rotation = 0
  ScaleType = 2
  TheoreticalExact = false
  Type = 1
  UnderTolerance = 0
  X = -5.73531
  Y = 23.4176
FEATURE [TechDraw::DrawViewDimension] Dimension018
  Arbitrary = false
  ArbitraryTolerances = false
  EqualTolerance = true
  FormatSpec = %.3f
  FormatSpecOverTolerance = %+.3f
  FormatSpecUnderTolerance = %+.3f
  Inverted = false
  LockPosition = false
  MeasureType = 1
  OverTolerance = 0
  References2D = -> [ProjItem003]
  Rotation = 0
  ScaleType = 2
  TheoreticalExact = true
  Type = 1
  UnderTolerance = 0
  X = -11.6996
  Y = -19.8319
FEATURE [TechDraw::DrawViewDimension] Dimension019
  Arbitrary = false
  ArbitraryTolerances = false
  EqualTolerance = true
  FormatSpec = %.3f
  FormatSpecOverTolerance = %+.3f
  FormatSpecUnderTolerance = %+.3f
  Inverted = false
  LockPosition = false
  MeasureType = 1
  OverTolerance = 0
  References2D = -> [ProjItem002]
  Rotation = 0
  ScaleType = 2
  TheoreticalExact = false
  Type = 0
  UnderTolerance = 0
  X = -24.6247
  Y = -11.4432
FEATURE [TechDraw::DrawViewDimension] Dimension025
  Arbitrary = false
  ArbitraryTolerances = false
  EqualTolerance = true
  FormatSpec = %.3f
  FormatSpecOverTolerance = %+.3f
  FormatSpecUnderTolerance = %+.3f
  Inverted = false
  LockPosition = false
  MeasureType = 1
  OverTolerance = 0
  References2D = -> [ProjItem]
  Rotation = 0
  ScaleType = 2
  TheoreticalExact = false
  Type = 1
  UnderTolerance = 0
  X = -44.2867
  Y = 37.5239
FEATURE [TechDraw::DrawViewDimension] Dimension026
  Arbitrary = false
  ArbitraryTolerances = false
  EqualTolerance = true
  FormatSpec = %.3f
  FormatSpecOverTolerance = %+.3f
  FormatSpecUnderTolerance = %+.3f
  Inverted = false
  LockPosition = false
  MeasureType = 1
  OverTolerance = 0
  References2D = -> [ProjItem]
  Rotation = 0
  ScaleType = 2
  TheoreticalExact = false
  Type = 1
  UnderTolerance = 0
  X = -37.8225
  Y = 28.538
FEATURE [TechDraw::DrawViewDimension] Dimension027
  Arbitrary = false
  ArbitraryTolerances = false
  EqualTolerance = true
  FormatSpec = %.3f
  FormatSpecOverTolerance = %+.3f
  FormatSpecUnderTolerance = %+.3f
  Inverted = false
  LockPosition = false
  MeasureType = 1
  OverTolerance = 0
  References2D = -> [ProjItem]
  Rotation = 0
  ScaleType = 2
  TheoreticalExact = false
  Type = 2
  UnderTolerance = 0
  X = 52.6325
  Y = 8.75614
FEATURE [TechDraw::DrawViewDimension] Dimension028
  Arbitrary = false
  ArbitraryTolerances = false
  EqualTolerance = true
  FormatSpec = ⌀%.3f
  FormatSpecOverTolerance = %+.3f
  FormatSpecUnderTolerance = %+.3f
  Inverted = false
  LockPosition = false
  MeasureType = 1
  OverTolerance = 0
  References2D = -> [ProjItem]
  Rotation = 0
  ScaleType = 2
  TheoreticalExact = false
  Type = 5
  UnderTolerance = 0
  X = -63.8005
  Y = 0.673949
FEATURE [TechDraw::DrawViewDimension] Dimension029
  Arbitrary = false
  ArbitraryTolerances = false
  EqualTolerance = true
  FormatSpec = %.3f
  FormatSpecOverTolerance = %+.3f
  FormatSpecUnderTolerance = %+.3f
  Inverted = false
  LockPosition = false
  MeasureType = 1
  OverTolerance = 0
  References2D = -> [ProjItem]
  Rotation = 0
  ScaleType = 2
  TheoreticalExact = false
  Type = 1
  UnderTolerance = 0
  X = -30.8843
  Y = -14.1999
FEATURE [TechDraw::DrawViewDimension] Dimension030
  Arbitrary = false
  ArbitraryTolerances = false
  EqualTolerance = true
  FormatSpec = %.3f
  FormatSpecOverTolerance = %+.3f
  FormatSpecUnderTolerance = %+.3f
  Inverted = false
  LockPosition = false
  MeasureType = 1
  OverTolerance = 0
  References2D = -> [ProjItem]
  Rotation = 0
  ScaleType = 2
  TheoreticalExact = false
  Type = 1
  UnderTolerance = 0
  X = 19.1734
  Y = -11.7288
FEATURE [TechDraw::DrawViewDimension] Dimension031
  Arbitrary = false
  ArbitraryTolerances = false
  EqualTolerance = true
  FormatSpec = %.3f
  FormatSpecOverTolerance = %+.3f
  FormatSpecUnderTolerance = %+.3f
  Inverted = false
  LockPosition = false
  MeasureType = 1
  OverTolerance = 0
  References2D = -> [ProjItem]
  Rotation = 0
  ScaleType = 2
  TheoreticalExact = false
  Type = 2
  UnderTolerance = 0
  X = 3.5771
  Y = 27.82
FEATURE [TechDraw::DrawViewDimension] Dimension032
  Arbitrary = false
  ArbitraryTolerances = false
  EqualTolerance = true
  FormatSpec = %.3f
  FormatSpecOverTolerance = %+.3f
  FormatSpecUnderTolerance = %+.3f
  Inverted = false
  LockPosition = false
  MeasureType = 1
  OverTolerance = 0
  References2D = -> [ProjItem]
  Rotation = 0
  ScaleType = 2
  TheoreticalExact = false
  Type = 2
  UnderTolerance = 0
  X = -13.6761
  Y = 28.0919
FEATURE [TechDraw::DrawPage] Page  label="PageFacePlate"
  KeepUpdated = true
  NextBalloonIndex = 1
  ProjectionType = 0
  Template = -> Template
  Views = -> [ProjGroup,Dimension,Dimension003,Dimension004,Dimension005,Dimension006,Dimension007,Dimension008,Dimension009,Dimension010,Dimension011,Dimension017,Dimension018,Dimension019,Dimension025,Dimension026,Dimension027,Dimension028,Dimension029,Dimension030,Dimension031,Dimension032]
note: 2 file-system paths scrubbed to <path> (originals preserved in the JSON sidecar)
